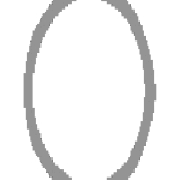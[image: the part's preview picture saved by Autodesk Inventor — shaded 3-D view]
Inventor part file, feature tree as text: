
AUTODESK INVENTOR PART (.ipt)
format: ipt  version: 2021 (Build 250183000, 183)  size: 109,056 bytes
history: native  units: in
note: dims shown in document units (in); Inventor stores cm internally (conversion verified against a paired STEP export)
features: other x4, sketch x3, plane x1
ambient origin geometry x8: Origin, YZ Plane, XZ Plane, XY Plane, X Axis, Y Axis, Z Axis, Center Point
bodies: Solid1 (feature_tree), Body (feature_tree)
feature tree (8):
  other  "Driven Length"
  other  "Frame Generator"
  other  "Start Plane"
  other  "End Plane"
  sketch  "Sketch"  dims[d2=20.0in d4=-0.0in d5=20.0in d6=0.12in d7=0.0in d8=90.0deg d9=20.0in]
  sketch  "Sketch2"  dims[d0=1.0in]
  plane  "Work Plane3"
  sketch  "Sketch3"  dims[d1=0.065in]
